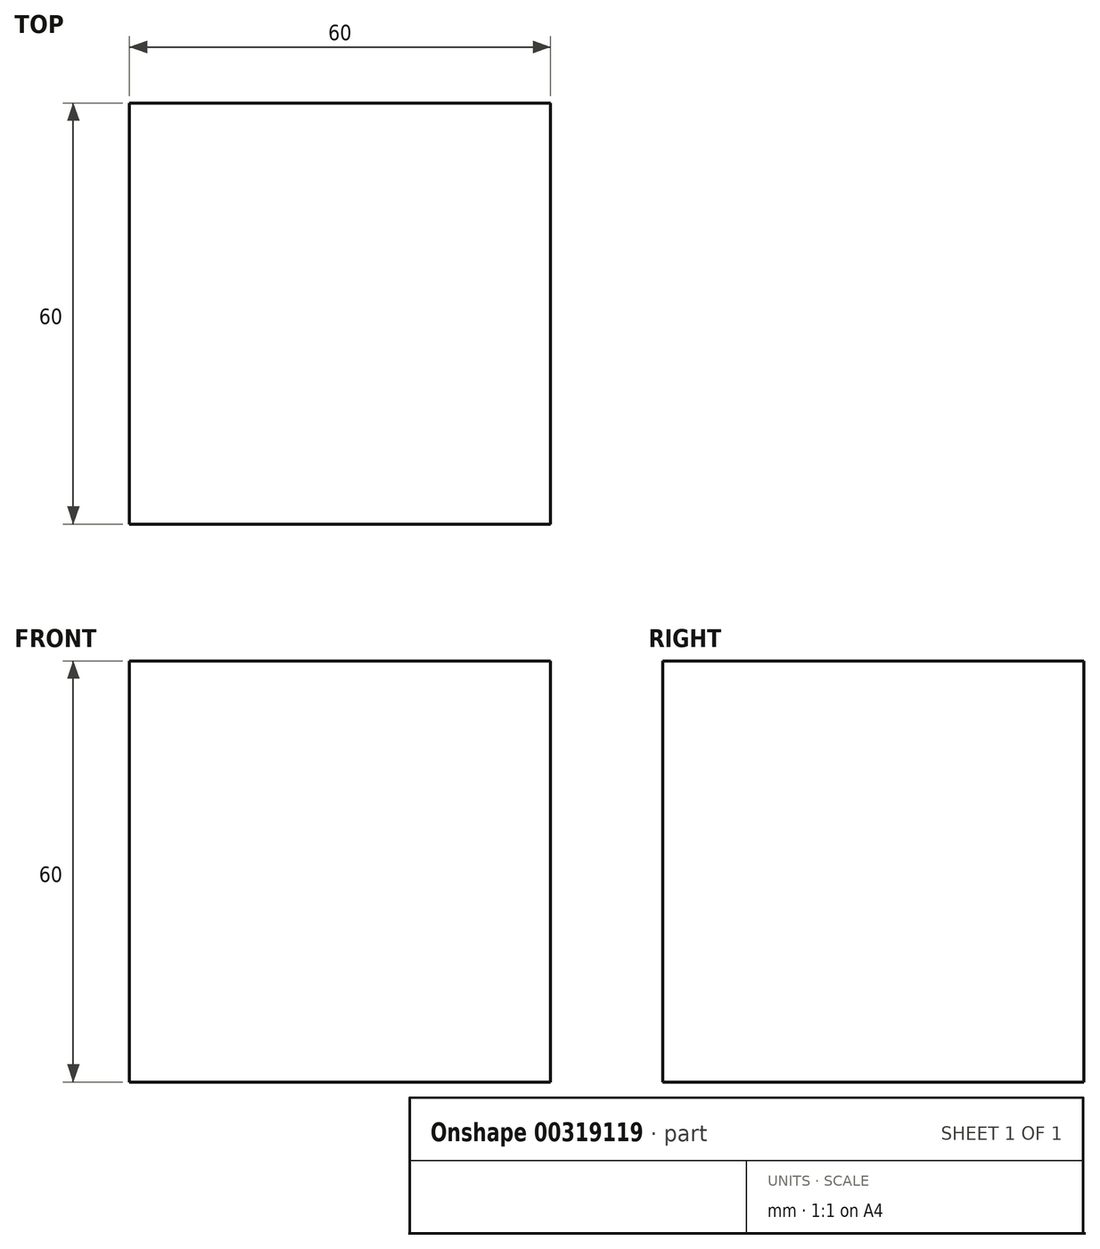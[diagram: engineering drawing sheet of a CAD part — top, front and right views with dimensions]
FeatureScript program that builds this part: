
annotation { "Feature Type Name" : "Feature", "Feature Type Description" : "" }
export const myFeature = defineFeature(function(context is Context, id is Id, definition is map)
    precondition{}
    {
        {
            var Q0;
            Q0=qCreatedBy(makeId("Front.planeOp"),FACE);
            var sketch = newSketch(context, id + "F0", { "sketchPlane" : qUnion([Q0])});
            skLineSegment(sketch, "E0.bottom", {"start": v(0, 0) * mm, "end": v(60, 0) * mm});
            skLineSegment(sketch, "E0.top", {"start": v(0, 60) * mm, "end": v(60, 60) * mm});
            skLineSegment(sketch, "E0.left", {"start": v(0, 0) * mm, "end": v(0, 60) * mm});
            skLineSegment(sketch, "E0.right", {"start": v(60, 0) * mm, "end": v(60, 60) * mm});
            skSolve(sketch);
        }
        {
            var Q0;
            Q0=makeQuery(id+"F0.imprint","IMPRINT",FACE,{"disambiguationData":[TD([[makeQuery(id+"F0.imprint","IMPRINT",EDGE,{"derivedFrom":sQuery(id+"F0.wireOp",EDGE,"E0.bottom")}),1.0]])]});
            extrude(context, id + "F1", {"entities" : qUnion([Q0]), "depth" : 60 * mm});
        }
    });
